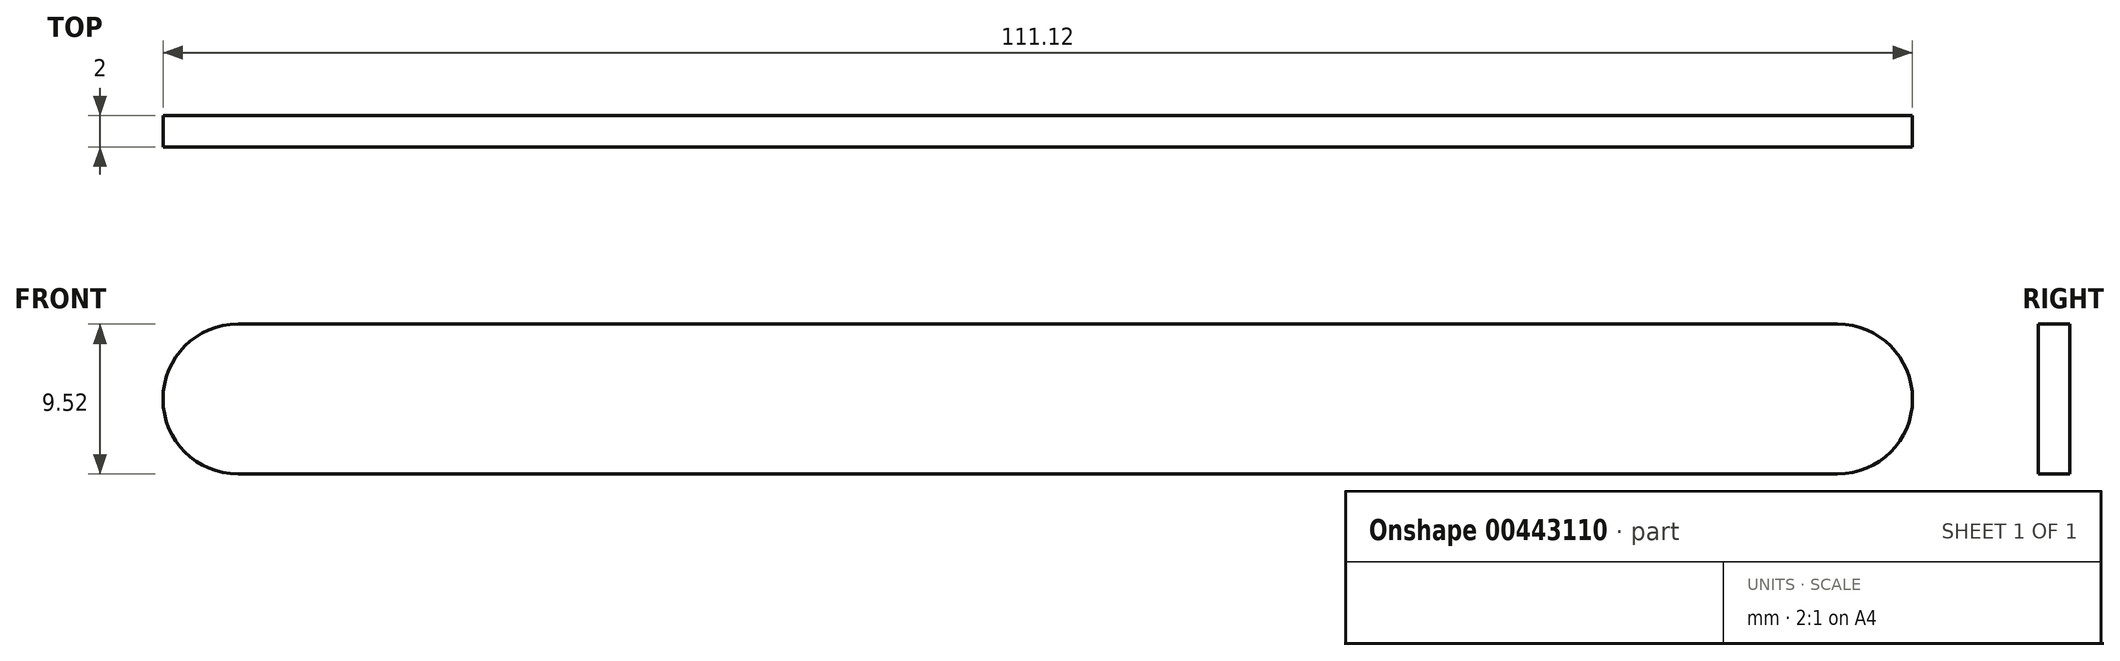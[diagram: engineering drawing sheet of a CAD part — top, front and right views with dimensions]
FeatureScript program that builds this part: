
annotation { "Feature Type Name" : "Feature", "Feature Type Description" : "" }
export const myFeature = defineFeature(function(context is Context, id is Id, definition is map)
    precondition{}
    {
        {
            var Q0;
            Q0=qCreatedBy(makeId("Front.planeOp"),FACE);
            var sketch = newSketch(context, id + "F0", { "sketchPlane" : qUnion([Q0])});
            skLineSegment(sketch, "E0.bottom", {"start": v(-61.33, 0.7) * mm, "end": v(40.27, 0.7) * mm});
            skLineSegment(sketch, "E0.top", {"start": v(-61.33, -8.82) * mm, "end": v(40.27, -8.82) * mm});
            skLineSegment(sketch, "E0.left", {"start": v(-61.33, 0.7) * mm, "end": v(-61.33, -8.82) * mm});
            skLineSegment(sketch, "E0.right", {"start": v(40.27, 0.7) * mm, "end": v(40.27, -8.82) * mm});
            skArc(sketch, "E1", {"start": v(-61.33, 0.7) * mm, "mid": v(-66.1, -4.06) * mm, "end": v(-61.33, -8.82) * mm});
            skArc(sketch, "E2", {"start": v(40.27, -8.82) * mm, "mid": v(45.03, -4.06) * mm, "end": v(40.27, 0.7) * mm});
            skSolve(sketch);
        }
        {
            var Q0;
            Q0 = qSketchRegion(id + "F0", true);
            extrude(context, id + "F1", {"entities" : qUnion([Q0]), "depth" : 2 * mm});
        }
    });
